# Revit family: DAL-A3-IntDbl-(6)
name_source: partatom
category: Doors
revit_build: Autodesk Revit 2016 (Build: 20150220_1215(x64)
units: mm (PartAtom-declared; Revit-internal decimal feet)

## family parameters
Always vertical = Yes
Cut with Voids When Loaded = No
Host = Wall
Room Calculation Point = No
Shared = No

## types (2) — shared parameters
Architrave Setback = 5 mm  [stored 0.0164042 ft]
Door Panel Height = 2060 mm
Door Panel Thickness = 32 mm  [stored 0.104987 ft]
Frame Thickness = 32 mm  [stored 0.104987 ft]
Function = Interior
Handle X Distance = 75 mm
Handle Z Distance = 1000 mm  [stored 3.28084 ft]
Height = 2110 mm  [stored 6.92257 ft]
Keynote = L20
Material Architrave = Door - Architrave
Material Door = Door - Panel
Material Frame = Door - Frame/Mullion
Material Glass = Door - Glazing
Material Ironmongery = Door - Handle
Operation = DoubleDoorSingleSwing
Rough Height = 2110 mm  [stored 6.92257 ft]
Stile Bottom Rail = 350 mm  [stored 1.14829 ft]
Stile Lock Rail = 175 mm  [stored 0.574147 ft]
Stile Shutting = 125 mm  [stored 0.410105 ft]
Stile Top Rail = 225 mm  [stored 0.738189 ft]
Stile Top of Lock Rail = 1100 mm
Stop Depth = 32 mm  [stored 0.104987 ft]
Stop Thickness = 19 mm  [stored 0.062336 ft]
Structural Tolerance = 8 mm  [stored 0.0262467 ft]
Thickness = 32 mm  [stored 0.104987 ft]
Tolerance = 3 mm  [stored 0.00984252 ft]
UnderCut = 7 mm  [stored 0.0229659 ft]
Vis - Ironmongery = Yes
VisionPanel Width = 200 mm  [stored 0.656168 ft]
Wall Closure = By host
zero-valued in all types: Door Panel Offset

## per-type parameters (varying)
| type | Door Panel Width | Rough Width | Width |
| 1810 x 2110mm | 861 mm | 1810 mm  [stored 5.93832 ft] | 1810 mm  [stored 5.93832 ft] |
| 1510 x 2110mm | 711 mm | 1510 mm  [stored 4.95407 ft] | 1510 mm  [stored 4.95407 ft] |

note: [stored X ft] marks values corroborated as IEEE doubles in the binary element streams (Revit-internal decimal feet)

## geometry (parser evidence)
native form markers: Sweep x4
no freeform markers — native parametric forms only
